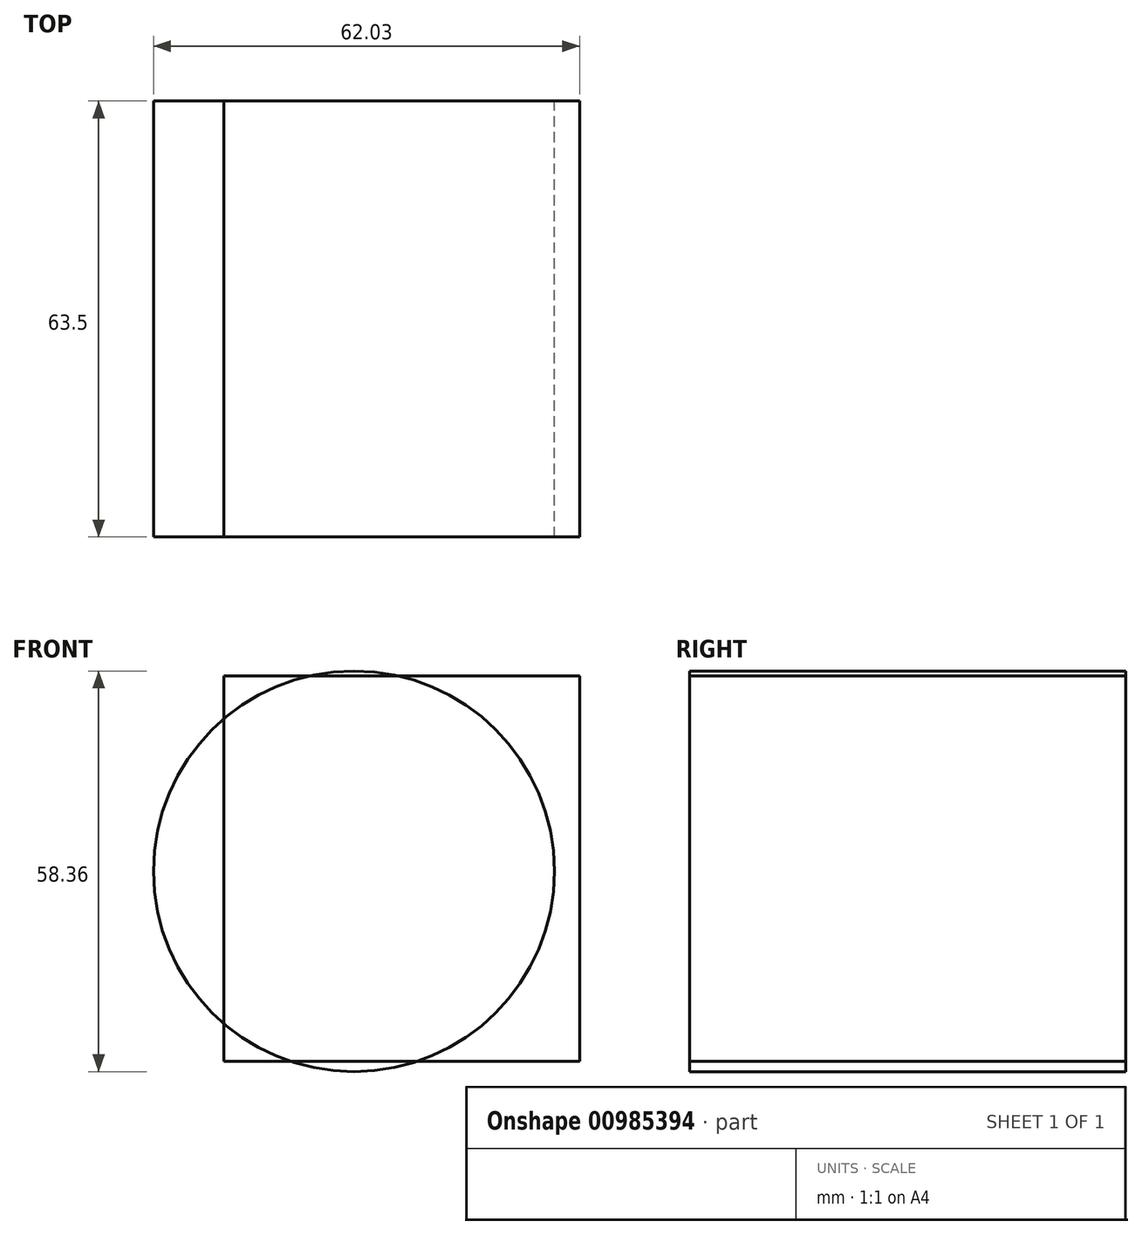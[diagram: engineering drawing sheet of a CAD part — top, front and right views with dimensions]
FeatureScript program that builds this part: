
annotation { "Feature Type Name" : "Feature", "Feature Type Description" : "" }
export const myFeature = defineFeature(function(context is Context, id is Id, definition is map)
    precondition{}
    {
        {
            var Q0;
            Q0=qCreatedBy(makeId("Front.planeOp"),FACE);
            var sketch = newSketch(context, id + "F0", { "sketchPlane" : qUnion([Q0])});
            skLineSegment(sketch, "E0.bottom", {"start": v(-18.92, 28.43) * mm, "end": v(32.85, 28.43) * mm});
            skLineSegment(sketch, "E0.top", {"start": v(-18.92, -27.66) * mm, "end": v(32.85, -27.66) * mm});
            skLineSegment(sketch, "E0.left", {"start": v(-18.92, 28.43) * mm, "end": v(-18.92, -27.66) * mm});
            skLineSegment(sketch, "E0.right", {"start": v(32.85, 28.43) * mm, "end": v(32.85, -27.66) * mm});
            skSolve(sketch);
        }
        {
            var Q0;
            Q0=makeQuery(id+"F0.imprint","IMPRINT",FACE,{"disambiguationData":[TD([[makeQuery(id+"F0.imprint","IMPRINT",EDGE,{"derivedFrom":sQuery(id+"F0.wireOp",EDGE,"E0.bottom")}),-1.0]])]});
            var sketch = newSketch(context, id + "F1", { "sketchPlane" : qUnion([Q0])});
            skCircle(sketch, "E1", {"center": v(0, 0) * mm, "radius": 29.18 * mm});
            skSolve(sketch);
        }
        {
            var Q0;
            Q0 = qSketchRegion(id + "F1", true);
            var Q1;
            Q1=makeQuery(id+"F0.imprint","IMPRINT",FACE,{"disambiguationData":[TD([[makeQuery(id+"F0.imprint","IMPRINT",EDGE,{"derivedFrom":sQuery(id+"F0.wireOp",EDGE,"E0.bottom")}),-1.0]])]});
            extrude(context, id + "F2", {"entities" : qUnion([Q0, Q1]), "depth" : 63.5 * mm, "offsetDistance" : 25.4 * mm});
        }
    });
